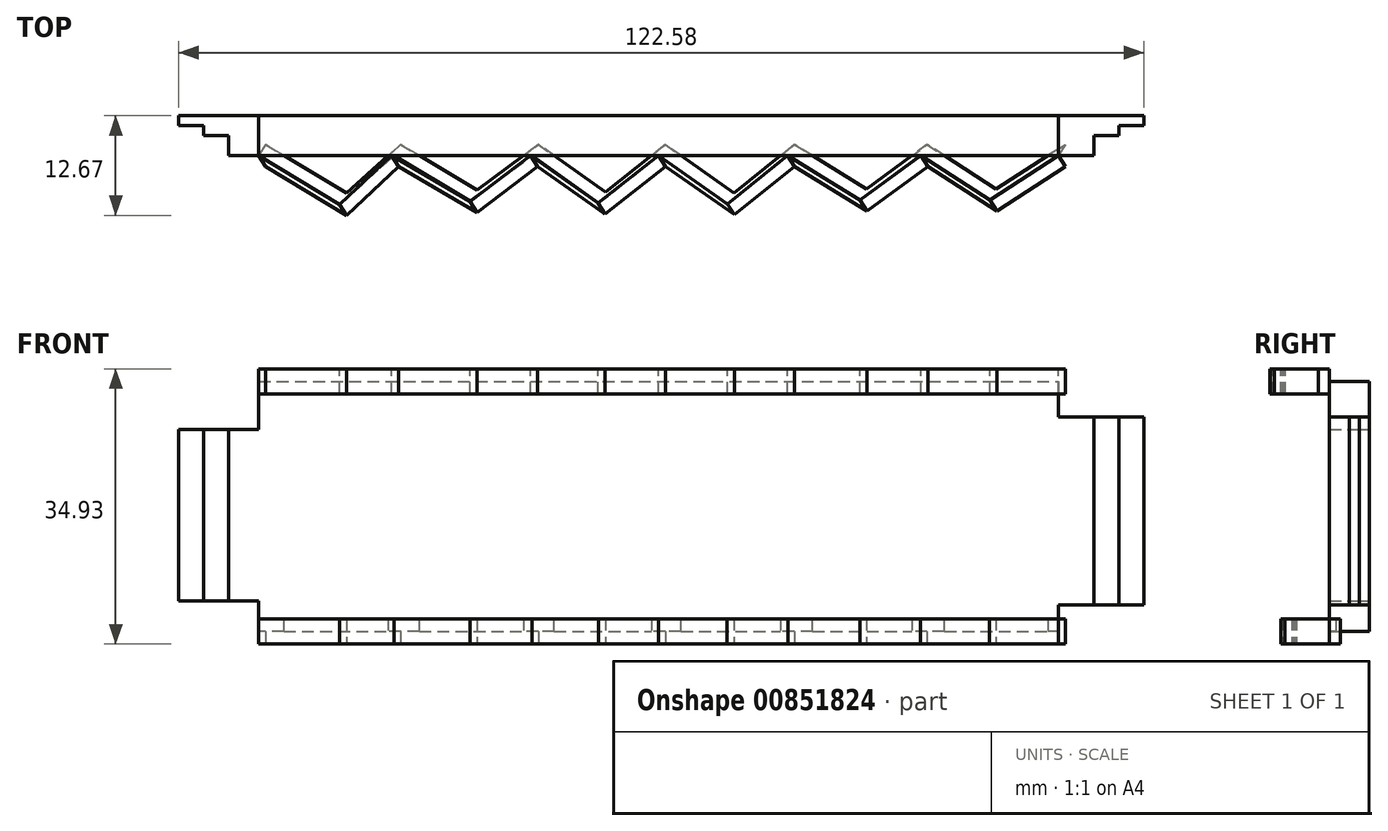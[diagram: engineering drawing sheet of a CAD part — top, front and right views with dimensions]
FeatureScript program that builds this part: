
annotation { "Feature Type Name" : "Feature", "Feature Type Description" : "" }
export const myFeature = defineFeature(function(context is Context, id is Id, definition is map)
    precondition{}
    {
        {
            var Q0;
            Q0=qCreatedBy(makeId("Front.planeOp"),FACE);
            var sketch = newSketch(context, id + "F0", { "sketchPlane" : qUnion([Q0])});
            skLineSegment(sketch, "E0.bottom", {"start": v(-60.98, 18.8) * mm, "end": v(40.62, 18.8) * mm});
            skLineSegment(sketch, "E0.top", {"start": v(-60.98, -12.94) * mm, "end": v(40.62, -12.94) * mm});
            skLineSegment(sketch, "E0.left", {"start": v(-60.98, 18.8) * mm, "end": v(-60.98, -12.94) * mm});
            skLineSegment(sketch, "E0.right", {"start": v(40.62, 18.8) * mm, "end": v(40.62, -12.94) * mm});
            skLineSegment(sketch, "E1.bottom", {"start": v(40.62, 14.3) * mm, "end": v(45.1, 14.3) * mm});
            skLineSegment(sketch, "E1.top", {"start": v(40.62, -9.6) * mm, "end": v(45.1, -9.6) * mm});
            skLineSegment(sketch, "E1.left", {"start": v(40.62, 14.3) * mm, "end": v(40.62, -9.6) * mm});
            skLineSegment(sketch, "E1.right", {"start": v(45.1, 14.3) * mm, "end": v(45.1, -9.6) * mm});
            skLineSegment(sketch, "E2.bottom", {"start": v(-60.98, 12.7) * mm, "end": v(-64.78, 12.7) * mm});
            skLineSegment(sketch, "E2.top", {"start": v(-60.98, -9.06) * mm, "end": v(-64.78, -9.06) * mm});
            skLineSegment(sketch, "E2.left", {"start": v(-60.98, 12.7) * mm, "end": v(-60.98, -9.06) * mm});
            skLineSegment(sketch, "E2.right", {"start": v(-64.78, 12.7) * mm, "end": v(-64.78, -9.06) * mm});
            skSolve(sketch);
        }
        {
            var Q0;
            Q0 = qSketchRegion(id + "F0", true);
            extrude(context, id + "F1", {"entities" : qUnion([Q0]), "depth" : 5.08 * mm, "offsetDistance" : 25.4 * mm});
        }
        {
            var Q0;
            Q0=makeQuery(id+"F1.opExtrude","SWEPT_FACE",FACE,{"disambiguationData":[OSD([sQuery(id+"F0.wireOp",EDGE,"E1.right")])]});
            var sketch = newSketch(context, id + "F2", { "sketchPlane" : qUnion([Q0])});
            skLineSegment(sketch, "E3.bottom", {"start": v(-2.54, 14.3) * mm, "end": v(0, 14.3) * mm});
            skLineSegment(sketch, "E3.top", {"start": v(-2.54, -9.6) * mm, "end": v(0, -9.6) * mm});
            skLineSegment(sketch, "E3.left", {"start": v(-2.54, 14.3) * mm, "end": v(-2.54, -9.6) * mm});
            skLineSegment(sketch, "E3.right", {"start": v(0, 14.3) * mm, "end": v(0, -9.6) * mm});
            skSolve(sketch);
        }
        {
            var Q0;
            Q0 = qSketchRegion(id + "F2", true);
            extrude(context, id + "F3", {"entities" : qUnion([Q0]), "operationType" : NewBodyOperationType.ADD, "depth" : 3.17 * mm, "offsetDistance" : 25.4 * mm});
        }
        {
            var Q0;
            Q0=makeQuery(id+"F3.opExtrude","CAP_FACE",FACE,{"disambiguationData":[OSD([sQuery(id+"F2.wireOp",EDGE,"E3.bottom"),sQuery(id+"F2.wireOp",EDGE,"E3.top"),sQuery(id+"F2.wireOp",EDGE,"E3.left"),sQuery(id+"F2.wireOp",EDGE,"E3.right")])],"isStart":false});
            var sketch = newSketch(context, id + "F4", { "sketchPlane" : qUnion([Q0])});
            skLineSegment(sketch, "E4.bottom", {"start": v(-1.27, 14.3) * mm, "end": v(0, 14.3) * mm});
            skLineSegment(sketch, "E4.top", {"start": v(-1.27, -9.6) * mm, "end": v(0, -9.6) * mm});
            skLineSegment(sketch, "E4.left", {"start": v(-1.27, 14.3) * mm, "end": v(-1.27, -9.6) * mm});
            skLineSegment(sketch, "E4.right", {"start": v(0, 14.3) * mm, "end": v(0, -9.6) * mm});
            skSolve(sketch);
        }
        {
            var Q0;
            Q0 = qSketchRegion(id + "F4", true);
            extrude(context, id + "F5", {"entities" : qUnion([Q0]), "operationType" : NewBodyOperationType.ADD, "depth" : 3.17 * mm, "offsetDistance" : 25.4 * mm});
        }
        {
            var Q0;
            Q0=makeQuery(id+"F1.opExtrude","SWEPT_FACE",FACE,{"disambiguationData":[OSD([sQuery(id+"F0.wireOp",EDGE,"E2.right")])]});
            var sketch = newSketch(context, id + "F6", { "sketchPlane" : qUnion([Q0])});
            skLineSegment(sketch, "E5.bottom", {"start": v(2.54, 12.7) * mm, "end": v(0, 12.7) * mm});
            skLineSegment(sketch, "E5.top", {"start": v(2.54, -9.06) * mm, "end": v(0, -9.06) * mm});
            skLineSegment(sketch, "E5.left", {"start": v(2.54, 12.7) * mm, "end": v(2.54, -9.06) * mm});
            skLineSegment(sketch, "E5.right", {"start": v(0, 12.7) * mm, "end": v(0, -9.06) * mm});
            skSolve(sketch);
        }
        {
            var Q0;
            Q0 = qSketchRegion(id + "F6", true);
            extrude(context, id + "F7", {"entities" : qUnion([Q0]), "operationType" : NewBodyOperationType.ADD, "depth" : 3.17 * mm, "offsetDistance" : 25.4 * mm});
        }
        {
            var Q0;
            Q0=makeQuery(id+"F7.opExtrude","CAP_FACE",FACE,{"disambiguationData":[OSD([sQuery(id+"F6.wireOp",EDGE,"E5.bottom"),sQuery(id+"F6.wireOp",EDGE,"E5.top"),sQuery(id+"F6.wireOp",EDGE,"E5.left"),sQuery(id+"F6.wireOp",EDGE,"E5.right")])],"isStart":false});
            var sketch = newSketch(context, id + "F8", { "sketchPlane" : qUnion([Q0])});
            skLineSegment(sketch, "E6.bottom", {"start": v(1.27, 12.7) * mm, "end": v(0, 12.7) * mm});
            skLineSegment(sketch, "E6.top", {"start": v(1.27, -9.06) * mm, "end": v(0, -9.06) * mm});
            skLineSegment(sketch, "E6.left", {"start": v(1.27, 12.7) * mm, "end": v(1.27, -9.06) * mm});
            skLineSegment(sketch, "E6.right", {"start": v(0, 12.7) * mm, "end": v(0, -9.06) * mm});
            skSolve(sketch);
        }
        {
            var Q0;
            Q0 = qSketchRegion(id + "F8", true);
            extrude(context, id + "F9", {"entities" : qUnion([Q0]), "operationType" : NewBodyOperationType.ADD, "depth" : 3.17 * mm, "offsetDistance" : 25.4 * mm});
        }
        {
            var Q0;
            Q0=makeQuery(id+"F1.opExtrude","SWEPT_FACE",FACE,{"disambiguationData":[OSD([sQuery(id+"F0.wireOp",EDGE,"E0.top")])]});
            var sketch = newSketch(context, id + "F10", { "sketchPlane" : qUnion([Q0])});
            skLineSegment(sketch, "E7", {"start": v(-60.98, 5.08) * mm, "end": v(-50.7, 11.26) * mm});
            skLineSegment(sketch, "E8", {"start": v(-50.7, 11.26) * mm, "end": v(-43.8, 5.08) * mm});
            skLineSegment(sketch, "E9", {"start": v(-43.8, 5.08) * mm, "end": v(-34.1, 10.86) * mm});
            skLineSegment(sketch, "E10", {"start": v(-34.1, 10.86) * mm, "end": v(-26.28, 5.08) * mm});
            skLineSegment(sketch, "E11", {"start": v(-26.28, 5.08) * mm, "end": v(-17.78, 11.13) * mm});
            skLineSegment(sketch, "E12", {"start": v(-17.78, 11.13) * mm, "end": v(-10.18, 5.08) * mm});
            skLineSegment(sketch, "E13", {"start": v(-10.18, 5.08) * mm, "end": v(-1.46, 11.26) * mm});
            skLineSegment(sketch, "E14", {"start": v(-1.46, 11.26) * mm, "end": v(6.24, 5.08) * mm});
            skLineSegment(sketch, "E15", {"start": v(6.24, 5.08) * mm, "end": v(15.4, 10.73) * mm});
            skLineSegment(sketch, "E16", {"start": v(15.4, 10.73) * mm, "end": v(23.09, 5.08) * mm});
            skLineSegment(sketch, "E17", {"start": v(23.09, 5.08) * mm, "end": v(31.85, 10.73) * mm});
            skLineSegment(sketch, "E18", {"start": v(31.85, 10.73) * mm, "end": v(40.62, 5.08) * mm});
            skSolve(sketch);
        }
        {
            var Q0;
            Q0 = qSketchRegion(id + "F10", true);
            var Q1;
            Q1=sQuery(id+"F10.wireOp",EDGE,"E7");
            var Q2;
            Q2=sQuery(id+"F10.wireOp",EDGE,"E8");
            var Q3;
            Q3=sQuery(id+"F10.wireOp",EDGE,"E9");
            var Q4;
            Q4=sQuery(id+"F10.wireOp",EDGE,"E10");
            var Q5;
            Q5=sQuery(id+"F10.wireOp",EDGE,"E11");
            var Q6;
            Q6=sQuery(id+"F10.wireOp",EDGE,"E12");
            var Q7;
            Q7=sQuery(id+"F10.wireOp",EDGE,"E13");
            var Q8;
            Q8=sQuery(id+"F10.wireOp",EDGE,"E14");
            var Q9;
            Q9=sQuery(id+"F10.wireOp",EDGE,"E15");
            var Q10;
            Q10=sQuery(id+"F10.wireOp",EDGE,"E16");
            var Q11;
            Q11=sQuery(id+"F10.wireOp",EDGE,"E18");
            var Q12;
            Q12=sQuery(id+"F10.wireOp",EDGE,"E17");
            extrude(context, id + "F11", {"entities" : qUnion([Q0]), "bodyType" : ToolBodyType.SURFACE, "surfaceEntities" : qUnion([Q1, Q2, Q3, Q4, Q5, Q6, Q7, Q8, Q9, Q10, Q11, Q12]), "endBound" : BoundingType.SYMMETRIC, "depth" : 3.17 * mm, "offsetDistance" : 25.4 * mm});
        }
        {
            var Q0;
            Q0=makeQuery(id+"F11.opExtrude","SWEPT_FACE",FACE,{"disambiguationData":[OSD([sQuery(id+"F10.wireOp",EDGE,"E7")])]});
            var Q1;
            Q1=makeQuery(id+"F11.opExtrude","SWEPT_FACE",FACE,{"disambiguationData":[OSD([sQuery(id+"F10.wireOp",EDGE,"E8")])]});
            var Q2;
            Q2=makeQuery(id+"F11.opExtrude","SWEPT_FACE",FACE,{"disambiguationData":[OSD([sQuery(id+"F10.wireOp",EDGE,"E9")])]});
            var Q3;
            Q3=makeQuery(id+"F11.opExtrude","SWEPT_FACE",FACE,{"disambiguationData":[OSD([sQuery(id+"F10.wireOp",EDGE,"E10")])]});
            var Q4;
            Q4=makeQuery(id+"F11.opExtrude","SWEPT_FACE",FACE,{"disambiguationData":[OSD([sQuery(id+"F10.wireOp",EDGE,"E11")])]});
            var Q5;
            Q5=makeQuery(id+"F11.opExtrude","SWEPT_FACE",FACE,{"disambiguationData":[OSD([sQuery(id+"F10.wireOp",EDGE,"E18")])]});
            var Q6;
            Q6=makeQuery(id+"F11.opExtrude","SWEPT_FACE",FACE,{"disambiguationData":[OSD([sQuery(id+"F10.wireOp",EDGE,"E17")])]});
            var Q7;
            Q7=makeQuery(id+"F11.opExtrude","SWEPT_FACE",FACE,{"disambiguationData":[OSD([sQuery(id+"F10.wireOp",EDGE,"E16")])]});
            var Q8;
            Q8=makeQuery(id+"F11.opExtrude","SWEPT_FACE",FACE,{"disambiguationData":[OSD([sQuery(id+"F10.wireOp",EDGE,"E15")])]});
            var Q9;
            Q9=makeQuery(id+"F11.opExtrude","SWEPT_FACE",FACE,{"disambiguationData":[OSD([sQuery(id+"F10.wireOp",EDGE,"E14")])]});
            var Q10;
            Q10=makeQuery(id+"F11.opExtrude","SWEPT_FACE",FACE,{"disambiguationData":[OSD([sQuery(id+"F10.wireOp",EDGE,"E13")])]});
            var Q11;
            Q11=makeQuery(id+"F11.opExtrude","SWEPT_FACE",FACE,{"disambiguationData":[OSD([sQuery(id+"F10.wireOp",EDGE,"E12")])]});
            extrude(context, id + "F12", {"entities" : qUnion([Q0, Q1, Q2, Q3, Q4, Q5, Q6, Q7, Q8, Q9, Q10, Q11]), "operationType" : NewBodyOperationType.ADD, "depth" : 1.65 * mm, "offsetDistance" : 25.4 * mm});
        }
        {
            var Q0;
            Q0=makeQuery(id+"F1.opExtrude","SWEPT_FACE",FACE,{"disambiguationData":[OSD([sQuery(id+"F0.wireOp",EDGE,"E0.bottom")])]});
            var sketch = newSketch(context, id + "F13", { "sketchPlane" : qUnion([Q0])});
            skLineSegment(sketch, "E19", {"start": v(-60.98, -5.08) * mm, "end": v(-50.7, -11.28) * mm});
            skLineSegment(sketch, "E20", {"start": v(-50.7, -11.28) * mm, "end": v(-44.1, -5.08) * mm});
            skLineSegment(sketch, "E21", {"start": v(-44.1, -5.08) * mm, "end": v(-34.13, -10.93) * mm});
            skLineSegment(sketch, "E22", {"start": v(-34.13, -10.93) * mm, "end": v(-26.47, -5.08) * mm});
            skLineSegment(sketch, "E23", {"start": v(-26.47, -5.08) * mm, "end": v(-17.88, -11.12) * mm});
            skLineSegment(sketch, "E24", {"start": v(-17.88, -11.12) * mm, "end": v(-10.18, -5.08) * mm});
            skLineSegment(sketch, "E25", {"start": v(-10.18, -5.08) * mm, "end": v(-1.43, -11.2) * mm});
            skLineSegment(sketch, "E26", {"start": v(-1.43, -11.2) * mm, "end": v(6.18, -5.08) * mm});
            skLineSegment(sketch, "E27", {"start": v(6.18, -5.08) * mm, "end": v(15.43, -10.7) * mm});
            skLineSegment(sketch, "E28", {"start": v(15.43, -10.7) * mm, "end": v(23.12, -5.08) * mm});
            skLineSegment(sketch, "E29", {"start": v(23.12, -5.08) * mm, "end": v(31.93, -10.71) * mm});
            skLineSegment(sketch, "E30", {"start": v(31.93, -10.71) * mm, "end": v(40.62, -5.08) * mm});
            skSolve(sketch);
        }
        {
            var Q0;
            Q0 = qSketchRegion(id + "F13", true);
            var Q1;
            Q1=sQuery(id+"F13.wireOp",EDGE,"E19");
            var Q2;
            Q2=sQuery(id+"F13.wireOp",EDGE,"E20");
            var Q3;
            Q3=sQuery(id+"F13.wireOp",EDGE,"E21");
            var Q4;
            Q4=sQuery(id+"F13.wireOp",EDGE,"E22");
            var Q5;
            Q5=sQuery(id+"F13.wireOp",EDGE,"E23");
            var Q6;
            Q6=sQuery(id+"F13.wireOp",EDGE,"E24");
            var Q7;
            Q7=sQuery(id+"F13.wireOp",EDGE,"E25");
            var Q8;
            Q8=sQuery(id+"F13.wireOp",EDGE,"E26");
            var Q9;
            Q9=sQuery(id+"F13.wireOp",EDGE,"E27");
            var Q10;
            Q10=sQuery(id+"F13.wireOp",EDGE,"E28");
            var Q11;
            Q11=sQuery(id+"F13.wireOp",EDGE,"E29");
            var Q12;
            Q12=sQuery(id+"F13.wireOp",EDGE,"E30");
            extrude(context, id + "F14", {"entities" : qUnion([Q0]), "bodyType" : ToolBodyType.SURFACE, "surfaceEntities" : qUnion([Q1, Q2, Q3, Q4, Q5, Q6, Q7, Q8, Q9, Q10, Q11, Q12]), "endBound" : BoundingType.SYMMETRIC, "depth" : 3.17 * mm, "offsetDistance" : 25.4 * mm});
        }
        {
            var Q0;
            Q0=makeQuery(id+"F14.opExtrude","SWEPT_FACE",FACE,{"disambiguationData":[OSD([sQuery(id+"F13.wireOp",EDGE,"E30")])]});
            var Q1;
            Q1=makeQuery(id+"F14.opExtrude","SWEPT_FACE",FACE,{"disambiguationData":[OSD([sQuery(id+"F13.wireOp",EDGE,"E29")])]});
            var Q2;
            Q2=makeQuery(id+"F14.opExtrude","SWEPT_FACE",FACE,{"disambiguationData":[OSD([sQuery(id+"F13.wireOp",EDGE,"E28")])]});
            var Q3;
            Q3=makeQuery(id+"F14.opExtrude","SWEPT_FACE",FACE,{"disambiguationData":[OSD([sQuery(id+"F13.wireOp",EDGE,"E27")])]});
            var Q4;
            Q4=makeQuery(id+"F14.opExtrude","SWEPT_FACE",FACE,{"disambiguationData":[OSD([sQuery(id+"F13.wireOp",EDGE,"E26")])]});
            var Q5;
            Q5=makeQuery(id+"F14.opExtrude","SWEPT_FACE",FACE,{"disambiguationData":[OSD([sQuery(id+"F13.wireOp",EDGE,"E25")])]});
            var Q6;
            Q6=makeQuery(id+"F14.opExtrude","SWEPT_FACE",FACE,{"disambiguationData":[OSD([sQuery(id+"F13.wireOp",EDGE,"E24")])]});
            var Q7;
            Q7=makeQuery(id+"F14.opExtrude","SWEPT_FACE",FACE,{"disambiguationData":[OSD([sQuery(id+"F13.wireOp",EDGE,"E23")])]});
            var Q8;
            Q8=makeQuery(id+"F14.opExtrude","SWEPT_FACE",FACE,{"disambiguationData":[OSD([sQuery(id+"F13.wireOp",EDGE,"E22")])]});
            var Q9;
            Q9=makeQuery(id+"F14.opExtrude","SWEPT_FACE",FACE,{"disambiguationData":[OSD([sQuery(id+"F13.wireOp",EDGE,"E21")])]});
            var Q10;
            Q10=makeQuery(id+"F14.opExtrude","SWEPT_FACE",FACE,{"disambiguationData":[OSD([sQuery(id+"F13.wireOp",EDGE,"E20")])]});
            var Q11;
            Q11=makeQuery(id+"F14.opExtrude","SWEPT_FACE",FACE,{"disambiguationData":[OSD([sQuery(id+"F13.wireOp",EDGE,"E19")])]});
            extrude(context, id + "F15", {"entities" : qUnion([Q0, Q1, Q2, Q3, Q4, Q5, Q6, Q7, Q8, Q9, Q10, Q11]), "depth" : 1.65 * mm, "offsetDistance" : 25.4 * mm});
        }
    });
